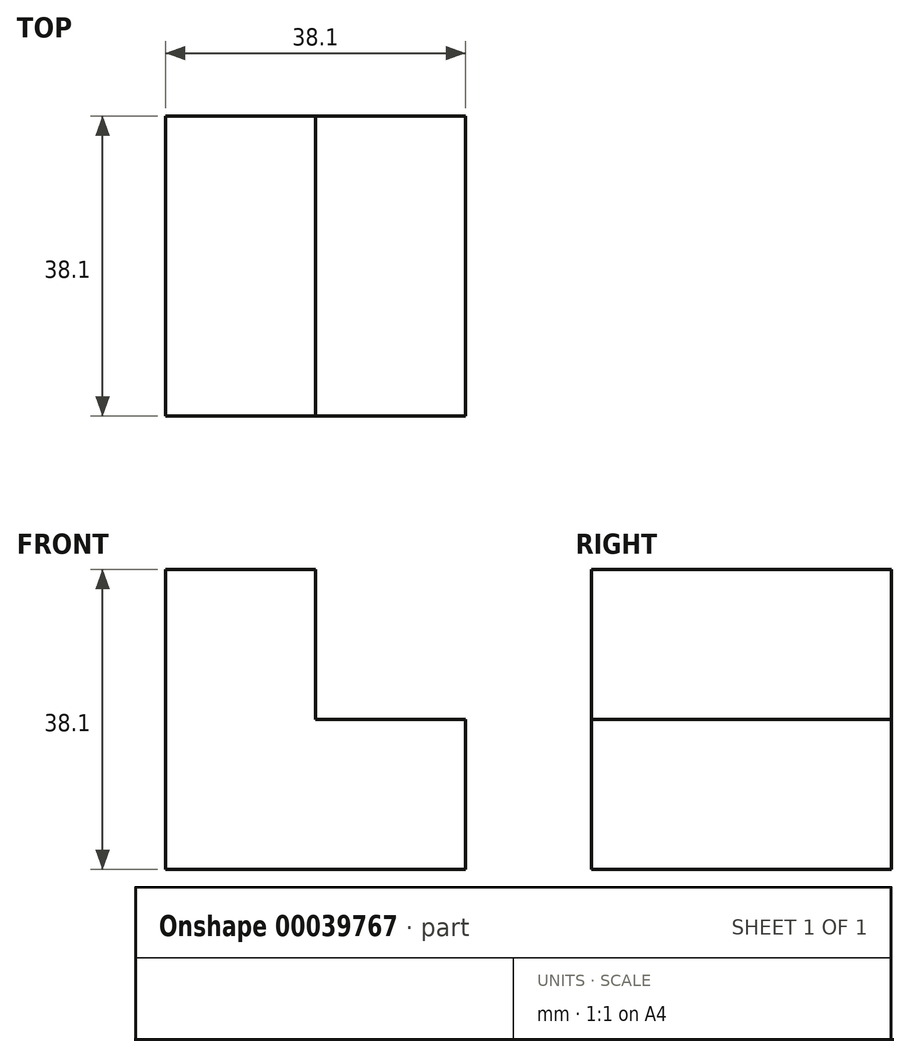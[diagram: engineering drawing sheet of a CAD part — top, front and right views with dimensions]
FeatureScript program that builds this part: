
annotation { "Feature Type Name" : "Feature", "Feature Type Description" : "" }
export const myFeature = defineFeature(function(context is Context, id is Id, definition is map)
    precondition{}
    {
        {
            var Q0;
            Q0=qCreatedBy(makeId("Top.planeOp"),FACE);
            var sketch = newSketch(context, id + "F0", { "sketchPlane" : qUnion([Q0])});
            skLineSegment(sketch, "E0.bottom", {"start": v(0, 0) * mm, "end": v(38.1, 0) * mm});
            skLineSegment(sketch, "E0.top", {"start": v(0, -38.1) * mm, "end": v(38.1, -38.1) * mm});
            skLineSegment(sketch, "E0.left", {"start": v(0, 0) * mm, "end": v(0, -38.1) * mm});
            skLineSegment(sketch, "E0.right", {"start": v(38.1, 0) * mm, "end": v(38.1, -38.1) * mm});
            skSolve(sketch);
        }
        {
            var Q0;
            Q0=makeQuery(id+"F0.imprint","IMPRINT",FACE,{"disambiguationData":[TD([[makeQuery(id+"F0.imprint","IMPRINT",EDGE,{"derivedFrom":sQuery(id+"F0.wireOp",EDGE,"E0.bottom")}),-1.0]])]});
            extrude(context, id + "F1", {"entities" : qUnion([Q0]), "depth" : 19.05 * mm});
        }
        {
            var Q0;
            Q0=makeQuery(id+"F1.opExtrude","CAP_FACE",FACE,{"disambiguationData":[OSD([sQuery(id+"F0.wireOp",EDGE,"E0.bottom"),sQuery(id+"F0.wireOp",EDGE,"E0.top"),sQuery(id+"F0.wireOp",EDGE,"E0.left"),sQuery(id+"F0.wireOp",EDGE,"E0.right")])],"isStart":false});
            var sketch = newSketch(context, id + "F2", { "sketchPlane" : qUnion([Q0])});
            skLineSegment(sketch, "E1.bottom", {"start": v(0, 0) * mm, "end": v(19.05, 0) * mm});
            skLineSegment(sketch, "E1.top", {"start": v(0, -38.1) * mm, "end": v(19.05, -38.1) * mm});
            skLineSegment(sketch, "E1.left", {"start": v(0, 0) * mm, "end": v(0, -38.1) * mm});
            skLineSegment(sketch, "E1.right", {"start": v(19.05, 0) * mm, "end": v(19.05, -38.1) * mm});
            skSolve(sketch);
        }
        {
            var Q0;
            Q0=makeQuery(id+"F2.imprint","IMPRINT",FACE,{"disambiguationData":[TD([[makeQuery(id+"F2.imprint","IMPRINT",EDGE,{"derivedFrom":sQuery(id+"F2.wireOp",EDGE,"E1.bottom")}),-1.0]])]});
            extrude(context, id + "F3", {"entities" : qUnion([Q0]), "operationType" : NewBodyOperationType.ADD, "depth" : 19.05 * mm});
        }
    });
